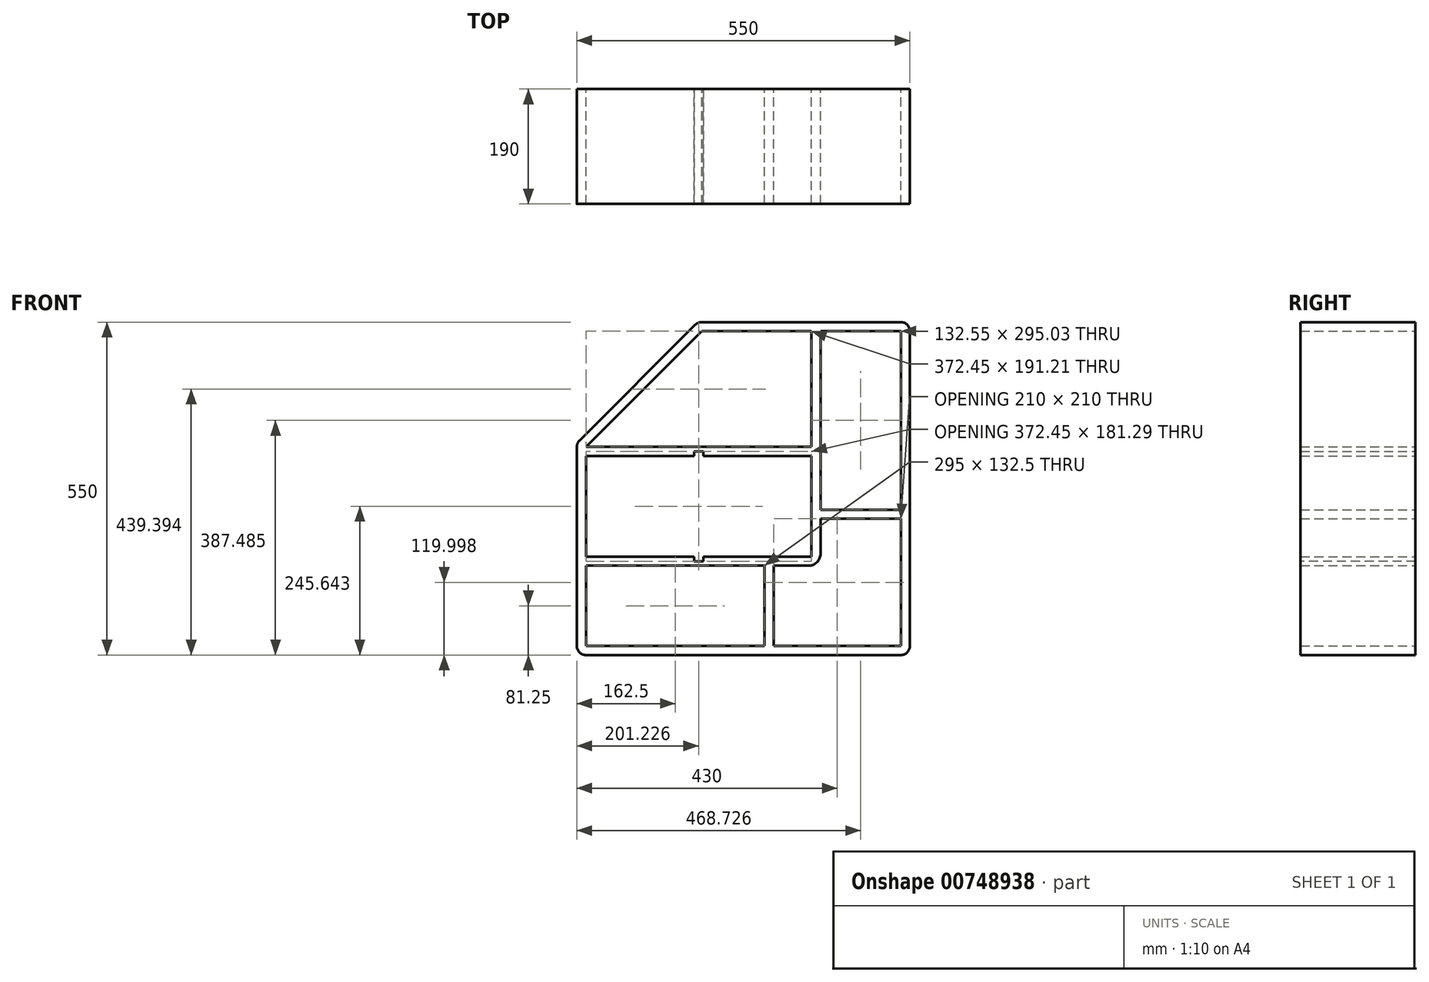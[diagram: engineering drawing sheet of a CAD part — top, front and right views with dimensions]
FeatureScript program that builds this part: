
annotation { "Feature Type Name" : "Feature", "Feature Type Description" : "" }
export const myFeature = defineFeature(function(context is Context, id is Id, definition is map)
    precondition{}
    {
        {
            var Q0;
            Q0=qCreatedBy(makeId("Front.planeOp"),FACE);
            var sketch = newSketch(context, id + "F0", { "sketchPlane" : qUnion([Q0])});
            skLineSegment(sketch, "E0.bottom", {"start": v(-68.83, 275) * mm, "end": v(260, 275) * mm});
            skLineSegment(sketch, "E0.top", {"start": v(-260, -275) * mm, "end": v(260, -275) * mm});
            skLineSegment(sketch, "E0.left", {"start": v(-275, 68.79) * mm, "end": v(-275, -260) * mm});
            skLineSegment(sketch, "E0.right", {"start": v(275, 260) * mm, "end": v(275, -260) * mm});
            skPoint(sketch, "E0.middle", {"position": v(0, 0) * mm});
            skLineSegment(sketch, "E1.bottom", {"start": v(-275, -275) * mm, "end": v(-375, -275) * mm, "construction": true});
            skLineSegment(sketch, "E1.top", {"start": v(-275, 75) * mm, "end": v(-375, 75) * mm, "construction": true});
            skLineSegment(sketch, "E1.right", {"start": v(-375, -275) * mm, "end": v(-375, 75) * mm, "construction": true});
            skLineSegment(sketch, "E2.MirrorCS", {"start": v(274.96, 375) * mm, "end": v(-75.04, 375) * mm, "construction": true});
            skLineSegment(sketch, "E3.MirrorCS", {"start": v(274.96, 275) * mm, "end": v(274.96, 375) * mm, "construction": true});
            skLineSegment(sketch, "E4.MirrorCS", {"start": v(-75.04, 275) * mm, "end": v(-75.04, 375) * mm, "construction": true});
            skLineSegment(sketch, "E5", {"start": v(-270.6, 79.4) * mm, "end": v(-79.44, 270.6) * mm});
            skLineSegment(sketch, "E6.0", {"start": v(-68.83, 260) * mm, "end": v(112.45, 260) * mm});
            skLineSegment(sketch, "E6.1", {"start": v(-260, 68.79) * mm, "end": v(-68.83, 260) * mm});
            skLineSegment(sketch, "E6.2", {"start": v(260, 260) * mm, "end": v(260, -35) * mm});
            skLineSegment(sketch, "E6.3", {"start": v(-260, -260) * mm, "end": v(35, -260) * mm});
            skLineSegment(sketch, "E6.4", {"start": v(-260, -127.5) * mm, "end": v(-260, -260) * mm});
            skLineSegment(sketch, "E7", {"start": v(260, -260) * mm, "end": v(50, -260) * mm, "construction": true});
            skLineSegment(sketch, "E8", {"start": v(35, -260) * mm, "end": v(35, -267.5) * mm});
            skLineSegment(sketch, "E9", {"start": v(50, -267.5) * mm, "end": v(50, -260) * mm});
            skLineSegment(sketch, "E10.trimOffspring", {"start": v(50, -260) * mm, "end": v(260, -260) * mm});
            skLineSegment(sketch, "E11.bottom", {"start": v(50, -267.5) * mm, "end": v(35, -267.5) * mm});
            skLineSegment(sketch, "E11.left", {"start": v(50, -267.5) * mm, "end": v(50, -127.5) * mm});
            skLineSegment(sketch, "E11.right", {"start": v(35, -267.5) * mm, "end": v(35, -127.5) * mm});
            skLineSegment(sketch, "E12", {"start": v(50, -127.5) * mm, "end": v(107.45, -127.5) * mm});
            skLineSegment(sketch, "E13.trimOffspring", {"start": v(112.45, -112.5) * mm, "end": v(-66.27, -112.5) * mm});
            skLineSegment(sketch, "E14", {"start": v(112.45, -112.5) * mm, "end": v(112.45, 53.79) * mm});
            skLineSegment(sketch, "E15", {"start": v(127.45, -107.5) * mm, "end": v(127.45, -50.03) * mm});
            skLineSegment(sketch, "E16", {"start": v(35, -127.5) * mm, "end": v(35, -120) * mm});
            skLineSegment(sketch, "E17", {"start": v(35, -120) * mm, "end": v(50, -120.05) * mm});
            skLineSegment(sketch, "E18", {"start": v(50, -127.5) * mm, "end": v(50, -120.05) * mm});
            skLineSegment(sketch, "E19", {"start": v(-260, 68.79) * mm, "end": v(-100, 68.79) * mm});
            skLineSegment(sketch, "E20", {"start": v(-260, -112.5) * mm, "end": v(-260, 53.79) * mm});
            skLineSegment(sketch, "E21", {"start": v(275, -275) * mm, "end": v(-224.92, 224.82) * mm, "construction": true});
            skLineSegment(sketch, "E22.MirrorCS", {"start": v(267.45, -50) * mm, "end": v(267.45, -35) * mm});
            skLineSegment(sketch, "E23.MirrorCS", {"start": v(267.45, -50) * mm, "end": v(127.45, -50.03) * mm});
            skLineSegment(sketch, "E24.MirrorCS", {"start": v(127.45, -50.03) * mm, "end": v(120, -50.03) * mm});
            skLineSegment(sketch, "E25.MirrorCS", {"start": v(119.95, -35.03) * mm, "end": v(120, -50.03) * mm});
            skLineSegment(sketch, "E26.MirrorCS", {"start": v(127.45, -35.03) * mm, "end": v(119.95, -35.03) * mm});
            skLineSegment(sketch, "E27.MirrorCS", {"start": v(267.45, -35) * mm, "end": v(127.45, -35.03) * mm});
            skLineSegment(sketch, "E28.trimOffspring", {"start": v(127.45, -35.03) * mm, "end": v(127.45, 260) * mm});
            skLineSegment(sketch, "E29.trimOffspring", {"start": v(260, -50) * mm, "end": v(260, -260) * mm});
            skLineSegment(sketch, "E30", {"start": v(35, -127.5) * mm, "end": v(-260, -127.5) * mm});
            skLineSegment(sketch, "E31", {"start": v(-260, -127.5) * mm, "end": v(-267.5, -127.5) * mm});
            skLineSegment(sketch, "E32", {"start": v(-267.5, -127.5) * mm, "end": v(-267.5, -112.5) * mm});
            skLineSegment(sketch, "E33", {"start": v(-267.5, -112.5) * mm, "end": v(-260, -112.5) * mm});
            skLineSegment(sketch, "E34", {"start": v(112.45, 260) * mm, "end": v(112.45, 267.5) * mm});
            skLineSegment(sketch, "E35", {"start": v(112.45, 267.5) * mm, "end": v(127.45, 267.5) * mm});
            skLineSegment(sketch, "E36", {"start": v(127.45, 267.5) * mm, "end": v(127.45, 260) * mm});
            skLineSegment(sketch, "E37.trimOffspring", {"start": v(127.45, 260) * mm, "end": v(260, 260) * mm});
            skLineSegment(sketch, "E38.trimOffspring", {"start": v(-47.55, 68.79) * mm, "end": v(112.45, 68.79) * mm});
            skPoint(sketch, "E39.visualSharp", {"position": v(-75.04, 275) * mm});
            skArc(sketch, "E39.filletArc", {"start": v(-68.83, 275) * mm, "mid": v(-74.57, 273.86) * mm, "end": v(-79.44, 270.6) * mm});
            skPoint(sketch, "E40.visualSharp", {"position": v(-275, 75) * mm});
            skArc(sketch, "E40.filletArc", {"start": v(-270.6, 79.4) * mm, "mid": v(-273.86, 74.53) * mm, "end": v(-275, 68.79) * mm});
            skPoint(sketch, "E41.visualSharp", {"position": v(275, 275) * mm});
            skArc(sketch, "E41.filletArc", {"start": v(275, 260) * mm, "mid": v(270.6, 270.6) * mm, "end": v(260, 275) * mm});
            skPoint(sketch, "E42.visualSharp", {"position": v(275, -275) * mm});
            skArc(sketch, "E42.filletArc", {"start": v(260, -275) * mm, "mid": v(270.6, -270.6) * mm, "end": v(275, -260) * mm});
            skPoint(sketch, "E43.visualSharp", {"position": v(-275, -275) * mm});
            skArc(sketch, "E43.filletArc", {"start": v(-275, -260) * mm, "mid": v(-270.6, -270.6) * mm, "end": v(-260, -275) * mm});
            skPoint(sketch, "E44.visualSharp", {"position": v(127.45, -127.5) * mm});
            skArc(sketch, "E44.filletArc", {"start": v(107.45, -127.5) * mm, "mid": v(121.6, -121.64) * mm, "end": v(127.45, -107.5) * mm});
            skLineSegment(sketch, "E45", {"start": v(21.81, 260) * mm, "end": v(21.81, 220) * mm});
            skLineSegment(sketch, "E46", {"start": v(112.45, 220) * mm, "end": v(-108.82, 220) * mm});
            skLineSegment(sketch, "E47", {"start": v(-100, 68.79) * mm, "end": v(-47.55, 68.79) * mm});
            skLineSegment(sketch, "E48.0", {"start": v(-47.55, 53.79) * mm, "end": v(112.45, 53.79) * mm});
            skLineSegment(sketch, "E48.1", {"start": v(-100, 53.79) * mm, "end": v(-81.27, 53.79) * mm});
            skLineSegment(sketch, "E48.2", {"start": v(-260, 53.79) * mm, "end": v(-100, 53.79) * mm});
            skLineSegment(sketch, "E49.trimOffspring", {"start": v(112.45, 68.79) * mm, "end": v(112.45, 260) * mm});
            skCircle(sketch, "E50", {"center": v(-166.89, -29.36) * mm, "radius": 65 * mm});
            skCircle(sketch, "E51", {"center": v(19.34, -29.36) * mm, "radius": 65 * mm});
            skLineSegment(sketch, "E52", {"start": v(-260, 53.79) * mm, "end": v(-267.5, 53.79) * mm});
            skLineSegment(sketch, "E53", {"start": v(-267.5, 53.79) * mm, "end": v(-267.5, 68.79) * mm});
            skLineSegment(sketch, "E54", {"start": v(-267.5, 68.79) * mm, "end": v(-260, 68.79) * mm});
            skLineSegment(sketch, "E55", {"start": v(112.45, 53.79) * mm, "end": v(119.95, 53.79) * mm});
            skLineSegment(sketch, "E56", {"start": v(119.95, 53.79) * mm, "end": v(119.95, 68.79) * mm});
            skLineSegment(sketch, "E57", {"start": v(119.95, 68.79) * mm, "end": v(112.45, 68.79) * mm});
            skLineSegment(sketch, "E58", {"start": v(-73.77, -120) * mm, "end": v(-66.27, -120) * mm});
            skLineSegment(sketch, "E59", {"start": v(-66.27, -120) * mm, "end": v(-66.27, -112.5) * mm});
            skLineSegment(sketch, "E60", {"start": v(-73.77, -120) * mm, "end": v(-81.27, -120) * mm});
            skLineSegment(sketch, "E61", {"start": v(-81.27, -120) * mm, "end": v(-81.27, -112.5) * mm});
            skLineSegment(sketch, "E62.trimOffspring", {"start": v(-81.27, -112.5) * mm, "end": v(-260, -112.5) * mm});
            skPoint(sketch, "E63.oppositeSnap0", {"position": v(-81.27, -116.25) * mm});
            skLineSegment(sketch, "E63.bottom", {"start": v(-66.27, -120) * mm, "end": v(-81.27, -120) * mm});
            skLineSegment(sketch, "E63.top", {"start": v(-66.27, 68.79) * mm, "end": v(-81.27, 68.79) * mm});
            skLineSegment(sketch, "E63.left", {"start": v(-66.27, -120) * mm, "end": v(-66.27, 53.79) * mm});
            skLineSegment(sketch, "E63.right", {"start": v(-81.27, -120) * mm, "end": v(-81.27, 53.79) * mm});
            skLineSegment(sketch, "E64.trimOffspring", {"start": v(-66.27, 53.79) * mm, "end": v(-47.55, 53.79) * mm});
            skLineSegment(sketch, "E65.top", {"start": v(-81.27, 61.29) * mm, "end": v(-66.27, 61.29) * mm});
            skLineSegment(sketch, "E65.left", {"start": v(-81.27, 53.79) * mm, "end": v(-81.27, 61.29) * mm});
            skLineSegment(sketch, "E65.right", {"start": v(-66.27, 53.79) * mm, "end": v(-66.27, 61.29) * mm});
            skSolve(sketch);
        }
        {
            var Q0;
            Q0=qSketchRegion(id+"F0",true);
            var Q1;
            {var subQ2=sQuery(id+"F0.wireOp",EDGE,"E63.bottom");Q1=makeQuery(id+"F0.imprint","IMPRINT",FACE,{"disambiguationData":[TD([[makeQuery(id+"F0.imprint","IMPRINT",EDGE,{"derivedFrom":subQ2}),-1.0]])]});}
            var Q2;
            {var subQ0=sQuery(id+"F0.wireOp",EDGE,"E19");Q2=makeQuery(id+"F0.imprint","IMPRINT",FACE,{"disambiguationData":[TD([[makeQuery(id+"F0.imprint","IMPRINT",EDGE,{"derivedFrom":subQ0}),-1.0]])]});}
            var Q3;
            Q3=makeQuery(id+"F0.imprint","IMPRINT",FACE,{"disambiguationData":[TD([[makeQuery(id+"F0.imprint","IMPRINT",EDGE,{"derivedFrom":sQuery(id+"F0.wireOp",EDGE,"E12")}),1.0]])]});
            var Q4;
            {var subQ1=sQuery(id+"F0.wireOp",EDGE,"E11.bottom");Q4=makeQuery(id+"F0.imprint","IMPRINT",FACE,{"disambiguationData":[TD([[makeQuery(id+"F0.imprint","IMPRINT",EDGE,{"derivedFrom":subQ1}),-1.0]])]});}
            var Q5;
            {var subQ3=sQuery(id+"F0.wireOp",EDGE,"E22.MirrorCS");Q5=makeQuery(id+"F0.imprint","IMPRINT",FACE,{"disambiguationData":[TD([[makeQuery(id+"F0.imprint","IMPRINT",EDGE,{"derivedFrom":subQ3}),1.0]])]});}
            extrude(context, id + "F1", {"entities" : qUnion([Q0, Q1, Q2, Q3, Q4, Q5]), "depth" : 190 * mm, "offsetDistance" : 25 * mm});
        }
    });
